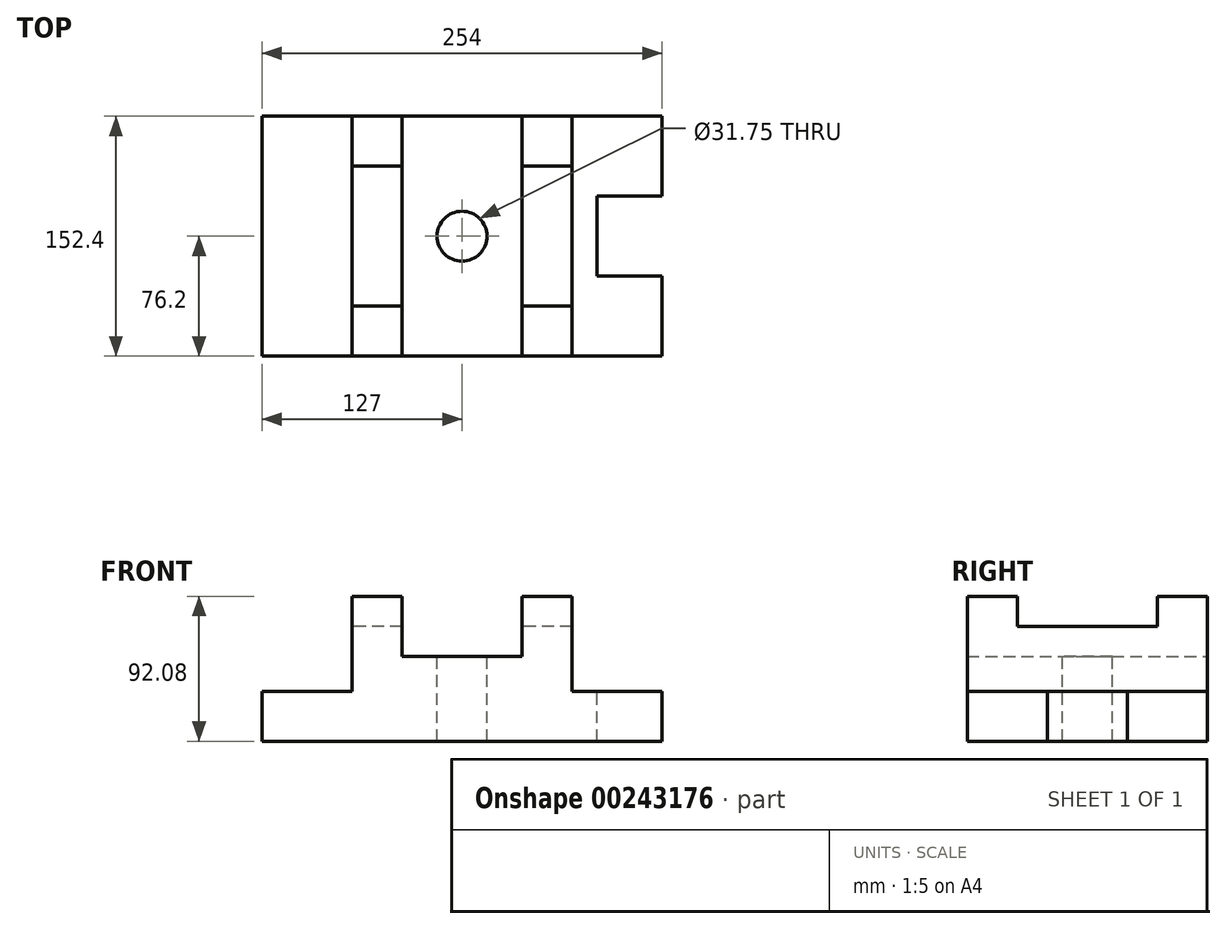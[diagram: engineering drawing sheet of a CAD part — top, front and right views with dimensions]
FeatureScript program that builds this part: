
annotation { "Feature Type Name" : "Feature", "Feature Type Description" : "" }
export const myFeature = defineFeature(function(context is Context, id is Id, definition is map)
    precondition{}
    {
        {
            var Q0;
            Q0=qCreatedBy(makeId("Front.planeOp"),FACE);
            var sketch = newSketch(context, id + "F0", { "sketchPlane" : qUnion([Q0])});
            skLineSegment(sketch, "E0", {"start": v(-127, 0) * mm, "end": v(-127, 31.75) * mm});
            skLineSegment(sketch, "E1", {"start": v(-127, 31.75) * mm, "end": v(-69.85, 31.75) * mm});
            skLineSegment(sketch, "E2", {"start": v(-69.85, 31.75) * mm, "end": v(-69.85, 92.07) * mm});
            skLineSegment(sketch, "E3", {"start": v(-69.85, 92.07) * mm, "end": v(-38.1, 92.07) * mm});
            skLineSegment(sketch, "E4", {"start": v(-38.1, 92.07) * mm, "end": v(-38.1, 53.97) * mm});
            skLineSegment(sketch, "E5", {"start": v(-38.1, 53.97) * mm, "end": v(38.1, 53.97) * mm});
            skLineSegment(sketch, "E6", {"start": v(38.1, 53.97) * mm, "end": v(38.1, 92.08) * mm});
            skLineSegment(sketch, "E7", {"start": v(38.1, 92.08) * mm, "end": v(69.85, 92.08) * mm});
            skLineSegment(sketch, "E8", {"start": v(69.85, 92.08) * mm, "end": v(69.85, 31.75) * mm});
            skLineSegment(sketch, "E9", {"start": v(69.85, 31.75) * mm, "end": v(127, 31.75) * mm});
            skLineSegment(sketch, "E10", {"start": v(127, 31.75) * mm, "end": v(127, 0) * mm});
            skLineSegment(sketch, "E11", {"start": v(127, 0) * mm, "end": v(-127, 0) * mm});
            skSolve(sketch);
        }
        {
            var Q0;
            Q0 = qSketchRegion(id + "F0", true);
            extrude(context, id + "F1", {"entities" : qUnion([Q0]), "depth" : 152.4 * mm});
        }
        {
            var Q0;
            Q0=makeQuery(id+"F1.opExtrude","SWEPT_FACE",FACE,{"disambiguationData":[OSD([sQuery(id+"F0.wireOp",EDGE,"E5")])]});
            var sketch = newSketch(context, id + "F2", { "sketchPlane" : qUnion([Q0])});
            skLineSegment(sketch, "E12", {"start": v(0, 0) * mm, "end": v(0, -152.4) * mm, "construction": true});
            skLineSegment(sketch, "E13", {"start": v(0, 0) * mm, "end": v(0, -76.2) * mm, "construction": true});
            skCircle(sketch, "E14", {"center": v(0, -76.2) * mm, "radius": 15.88 * mm});
            skSolve(sketch);
        }
        {
            var Q0;
            Q0=makeQuery(id+"F2.imprint","IMPRINT",FACE,{"disambiguationData":[TD([[makeQuery(id+"F2.imprint","IMPRINT",EDGE,{"derivedFrom":sQuery(id+"F2.wireOp",EDGE,"E14")}),1.0]])]});
            var Q1;
            Q1=sQuery(id+"F2.wireOp",EDGE,"E14");
            extrude(context, id + "F3", {"entities" : qUnion([Q0]), "operationType" : NewBodyOperationType.REMOVE, "surfaceEntities" : qUnion([Q1]), "endBound" : BoundingType.THROUGH_ALL, "oppositeDirection" : true, "depth" : 25.4 * mm});
        }
        {
            var Q0;
            Q0=makeQuery(id+"F1.opExtrude","SWEPT_FACE",FACE,{"disambiguationData":[OSD([sQuery(id+"F0.wireOp",EDGE,"E1")])]});
            var sketch = newSketch(context, id + "F4", { "sketchPlane" : qUnion([Q0])});
            skLineSegment(sketch, "E15", {"start": v(0, 0) * mm, "end": v(0, -152.4) * mm, "construction": true});
            skLineSegment(sketch, "E16", {"start": v(0, 0) * mm, "end": v(0, -76.2) * mm, "construction": true});
            skLineSegment(sketch, "E17", {"start": v(0, -76.2) * mm, "end": v(-127, -76.2) * mm, "construction": true});
            skLineSegment(sketch, "E18.bottom", {"start": v(-85.72, -101.6) * mm, "end": v(-127, -101.6) * mm});
            skLineSegment(sketch, "E18.top", {"start": v(-85.72, -50.8) * mm, "end": v(-127, -50.8) * mm});
            skLineSegment(sketch, "E18.left", {"start": v(-85.72, -101.6) * mm, "end": v(-85.72, -50.8) * mm});
            skPoint(sketch, "E18.middle", {"position": v(-127, -76.2) * mm});
            skLineSegment(sketch, "E19", {"start": v(-127, -50.8) * mm, "end": v(-127, -101.6) * mm});
            skLineSegment(sketch, "E20.bottom", {"start": v(-127, -50.8) * mm, "end": v(-85.72, -50.8) * mm});
            skLineSegment(sketch, "E20.top", {"start": v(-127, -101.6) * mm, "end": v(-85.72, -101.6) * mm});
            skLineSegment(sketch, "E20.right", {"start": v(-85.72, -50.8) * mm, "end": v(-85.72, -101.6) * mm});
            skLineSegment(sketch, "E21.MirrorCS", {"start": v(85.72, -50.8) * mm, "end": v(127, -50.8) * mm});
            skLineSegment(sketch, "E22.MirrorCS", {"start": v(85.72, -101.6) * mm, "end": v(85.72, -50.8) * mm});
            skLineSegment(sketch, "E23.MirrorCS", {"start": v(85.72, -101.6) * mm, "end": v(127, -101.6) * mm});
            skLineSegment(sketch, "E24.MirrorCS", {"start": v(127, -50.8) * mm, "end": v(127, -101.6) * mm});
            skSolve(sketch);
        }
        {
            var Q0;
            Q0=makeQuery(id+"F4.imprint","IMPRINT",FACE,{"disambiguationData":[TD([[makeQuery(id+"F4.imprint","IMPRINT",EDGE,{"derivedFrom":sQuery(id+"F4.wireOp",EDGE,"E20.bottom")}),-1.0]])]});
            var Q1;
            Q1=makeQuery(id+"F4.imprint","IMPRINT",FACE,{"disambiguationData":[TD([[makeQuery(id+"F4.imprint","IMPRINT",EDGE,{"derivedFrom":sQuery(id+"F4.wireOp",EDGE,"E21.MirrorCS")}),-1.0]])]});
            extrude(context, id + "F5", {"entities" : qUnion([Q0, Q1]), "operationType" : NewBodyOperationType.REMOVE, "endBound" : BoundingType.THROUGH_ALL, "oppositeDirection" : true, "depth" : 25.4 * mm});
        }
        {
            var Q0;
            Q0=makeQuery(id+"F1.opExtrude","SWEPT_FACE",FACE,{"disambiguationData":[OSD([sQuery(id+"F0.wireOp",EDGE,"E2")])]});
            var sketch = newSketch(context, id + "F6", { "sketchPlane" : qUnion([Q0])});
            skPoint(sketch, "E25", {"position": v(76.2, 92.08) * mm});
            skLineSegment(sketch, "E26", {"start": v(31.75, 92.08) * mm, "end": v(120.65, 92.08) * mm});
            skLineSegment(sketch, "E27", {"start": v(31.75, 92.08) * mm, "end": v(31.75, 73.03) * mm});
            skLineSegment(sketch, "E28", {"start": v(31.75, 73.03) * mm, "end": v(120.65, 73.03) * mm});
            skLineSegment(sketch, "E29", {"start": v(120.65, 73.03) * mm, "end": v(120.65, 92.08) * mm});
            skSolve(sketch);
        }
        {
            var Q0;
            Q0 = qSketchRegion(id + "F6", true);
            extrude(context, id + "F7", {"entities" : qUnion([Q0]), "operationType" : NewBodyOperationType.REMOVE, "endBound" : BoundingType.THROUGH_ALL, "oppositeDirection" : true, "depth" : 25.4 * mm});
        }
    });
